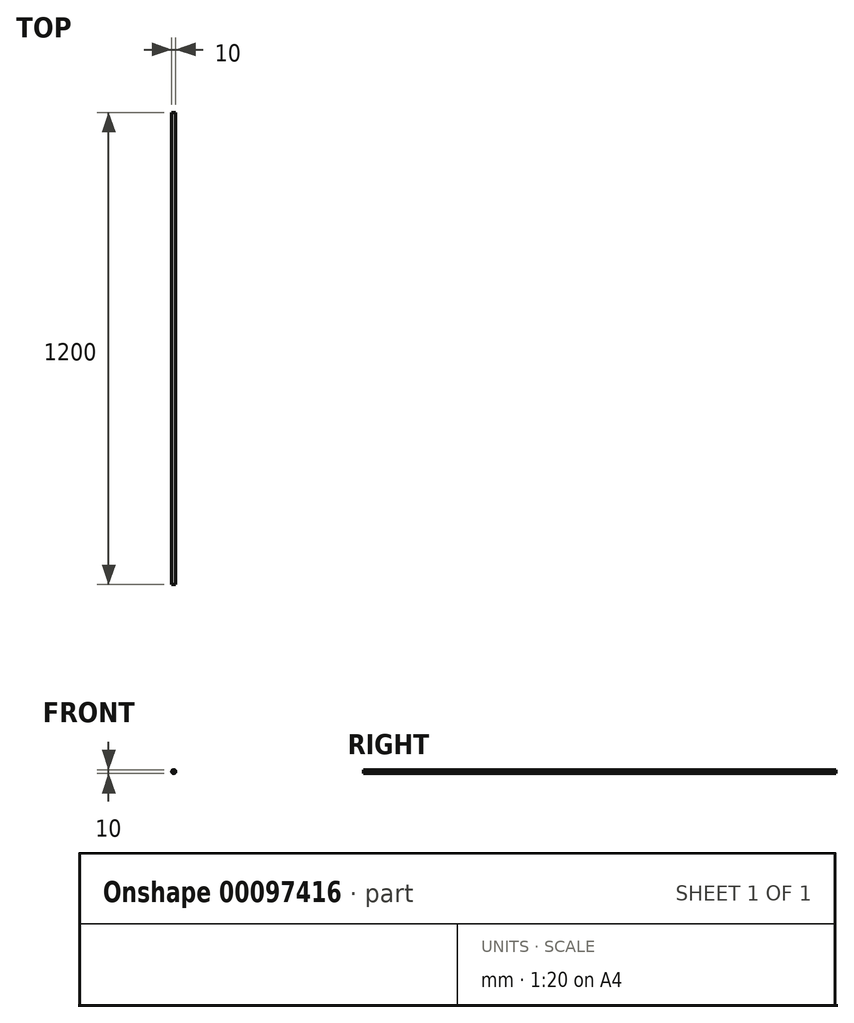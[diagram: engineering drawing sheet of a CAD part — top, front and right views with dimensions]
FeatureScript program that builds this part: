
annotation { "Feature Type Name" : "Feature", "Feature Type Description" : "" }
export const myFeature = defineFeature(function(context is Context, id is Id, definition is map)
    precondition{}
    {
        {
            var Q0;
            Q0=qCreatedBy(makeId("Front.planeOp"),FACE);
            var sketch = newSketch(context, id + "F0", { "sketchPlane" : qUnion([Q0])});
            skCircle(sketch, "E0", {"center": v(0, 0) * mm, "radius": 5 * mm});
            skSolve(sketch);
        }
        {
            var Q0;
            Q0 = qSketchRegion(id + "F0", true);
            extrude(context, id + "F1", {"entities" : qUnion([Q0]), "depth" : 1200 * mm});
        }
    });
